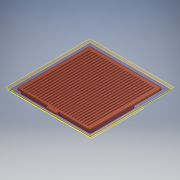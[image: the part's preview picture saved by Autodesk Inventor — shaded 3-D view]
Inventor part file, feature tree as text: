
AUTODESK INVENTOR PART (.ipt)
format: ipt  version: 2019 (Build 230136000, 136)  size: 586,240 bytes
history: native  units: mm
features: move_body x15, direct_edit x12, reference x11, sketch x8, extrude x7, other x5, plane x3, fillet x3, chamfer x1, projected_geometry x1
ambient origin geometry x8: Origin, YZ Plane, XZ Plane, XY Plane, X Axis, Y Axis, Z Axis, Center Point
bodies: Solid1 (feature_tree)
feature tree (66):
  plane  "Work Plane1"
  extrude  "Extrusion1"  Depth=2.0mm
  sketch  "Sketch2"  dims[d3=5.5mm d4=2.0mm]
  plane  "Work Plane2"
  plane  "Work Plane3"
  extrude  "Extrusion2"  Depth=2.0mm
  extrude  "Extrusion3"  Depth=1.0mm
  extrude  "Extrusion4"  Depth=1.5mm TaperAngle=0.0deg
  extrude  "Extrusion5"  Depth=1.0mm TaperAngle=0.0deg
  fillet  "Fillet1"  Radius=1.75mm
  direct_edit  "Direct Edit1"
  fillet  "Fillet2"  Radius=1.0mm
  direct_edit  "Direct Edit2"
  direct_edit  "Direct Edit3"
  direct_edit  "Direct Edit4"
  direct_edit  "Direct Edit5"
  direct_edit  "Direct Edit6"
  direct_edit  "Direct Edit7"
  direct_edit  "Direct Edit8"
  direct_edit  "Direct Edit9"
  direct_edit  "Direct Edit10"
  chamfer  "Chamfer2"  Distance=15.5mm
  direct_edit  "Direct Edit11"
  sketch  "Sketch6"  dims[d23=2.0mm d24=0.0mm d25=0.0mm d26=15.5mm]
  direct_edit  "Direct Edit12"
  extrude  "Extrusion6"  Depth=0.5mm TaperAngle=0.0deg
  fillet  "Fillet3"  Radius=2.5mm
  extrude  "Extrusion7"  TaperAngle=0.0deg  [1 undecoded]
  sketch  "Sketch1"  dims[d0=2.0mm d1=0.0mm d2=5.5mm]
  reference  "Reference2"
  sketch  "Sketch3"  dims[d5=1.0mm d6=0.0mm d7=1.0mm]
  reference  "Reference3"
  reference  "Reference4"
  reference  "Reference5"
  reference  "Reference6"
  reference  "Reference7"
  reference  "Reference8"
  reference  "Reference9"
  reference  "Reference10"
  reference  "Reference11"
  reference  "Reference12"
  sketch  "Sketch4"  dims[d8=100.0mm d10=7.62mm d11=10.0mm d13=10.0mm d15=1.5mm d16=0.0mm]
  sketch  "Sketch5"  dims[d17=1.5mm d18=3.75mm d19=0.0mm d20=1.75mm d21=0.0mm d22=1.0mm]
  sketch  "Sketch7"  dims[d27=0.0mm d28=0.0mm d29=-5.5mm d30=0.0mm d31=0.0mm d32=0.5mm]
  sketch  "Sketch8"  dims[d33=0.0mm d34=0.0mm d35=-4.0mm d36=0.0mm d37=0.0mm d38=2.5mm d39=0.0mm d40=0.0mm d41=-0.5mm d42=0.0mm d43=0.0mm d44=0.5mm d45=0.0mm d46=0.0mm d47=-0.5mm d48=0.0mm d49=0.0mm d50=-0.5mm d51=0.0mm d52=0.0mm d53=-0.5mm d57=0.0mm d58=0.0mm d59=-0.5mm d60=0.0mm d61=0.0mm d62=-0.9mm d63=0.0mm d64=0.0mm d65=-0.5mm d66=0.5mm d67=1.0mm d68=45.0deg d69=0.0mm d70=0.0mm d71=-13.0mm d72=0.0mm d73=0.0mm d74=0.6mm d75=13.0mm d76=6.0mm d77=1.5mm d78=0.0mm d79=2.0mm d80=1.0mm d81=78.0mm d82=260.0mm d84=3.0mm d85=10.0mm d87=10.0mm d89=0.3mm d90=0.0mm]
  projected_geometry  "Projected Loop1"
  parser-record x2  (decoder bookkeeping rows leaked as tree rows — omitted from the tree; the rows remain in map.json)
  other  "protoswitchboard.iam"
  other  "cover:1"
  other  "Delete1"
  move_body  "Move1"
  move_body  "Move2"
  move_body  "Move3"
  move_body  "Move4"
  move_body  "Move5"
  move_body  "Move6"
  move_body  "Move7"
  move_body  "Move8"
  move_body  "Move9"
  move_body  "Move10"
  move_body  "Move11"
  move_body  "Move12"
  move_body  "Move13"
  move_body  "Move14"
  move_body  "Move15"
note: 1 required parameter value undecoded (feature->parameter linkage not recoverable at this tier; creation-order binding heuristic only, values carry confidence <= 0.55)
note: 2 file-system paths scrubbed to <path> (originals preserved in map.json)
